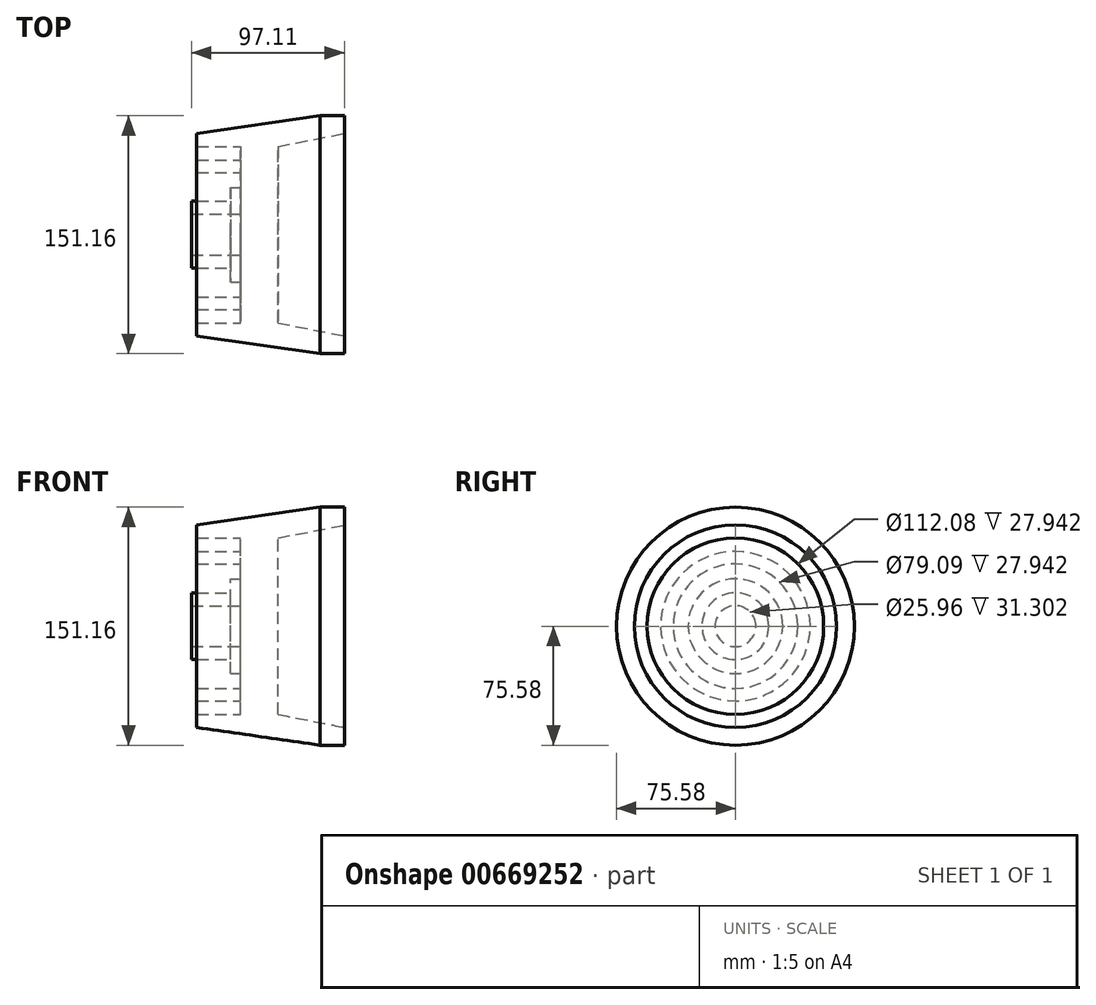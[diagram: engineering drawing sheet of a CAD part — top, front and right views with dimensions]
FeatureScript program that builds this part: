
annotation { "Feature Type Name" : "Feature", "Feature Type Description" : "" }
export const myFeature = defineFeature(function(context is Context, id is Id, definition is map)
    precondition{}
    {
        {
            var Q0;
            Q0=qCreatedBy(makeId("Front.planeOp"),FACE);
            var sketch = newSketch(context, id + "F0", { "sketchPlane" : qUnion([Q0])});
            skLineSegment(sketch, "E0", {"start": v(0, 0) * mm, "end": v(0, 12.98) * mm});
            skLineSegment(sketch, "E1", {"start": v(0, 12.98) * mm, "end": v(-31.3, 12.98) * mm});
            skLineSegment(sketch, "E2", {"start": v(-31.3, 12.98) * mm, "end": v(-31.3, 21.22) * mm});
            skLineSegment(sketch, "E3", {"start": v(-31.3, 21.22) * mm, "end": v(-6.57, 21.22) * mm});
            skLineSegment(sketch, "E4", {"start": v(-6.57, 21.22) * mm, "end": v(-6.57, 30.08) * mm});
            skLineSegment(sketch, "E5", {"start": v(-6.57, 30.08) * mm, "end": v(0, 30.08) * mm});
            skLineSegment(sketch, "E6", {"start": v(0, 30.08) * mm, "end": v(0, 39.55) * mm});
            skLineSegment(sketch, "E7", {"start": v(0, 39.55) * mm, "end": v(-27.94, 39.55) * mm});
            skLineSegment(sketch, "E8", {"start": v(-27.94, 39.55) * mm, "end": v(-27.94, 47.49) * mm});
            skLineSegment(sketch, "E9", {"start": v(-27.94, 47.49) * mm, "end": v(0, 47.49) * mm});
            skLineSegment(sketch, "E10", {"start": v(0, 47.49) * mm, "end": v(0, 56.04) * mm});
            skLineSegment(sketch, "E11", {"start": v(0, 56.04) * mm, "end": v(-27.94, 56.04) * mm});
            skLineSegment(sketch, "E12", {"start": v(-27.94, 56.04) * mm, "end": v(-27.94, 64.28) * mm});
            skLineSegment(sketch, "E13", {"start": v(-27.94, 64.28) * mm, "end": v(50.24, 75.58) * mm});
            skLineSegment(sketch, "E14", {"start": v(50.24, 75.58) * mm, "end": v(65.8, 75.58) * mm});
            skLineSegment(sketch, "E15", {"start": v(65.8, 75.58) * mm, "end": v(65.8, 64.28) * mm});
            skLineSegment(sketch, "E16", {"start": v(65.8, 64.28) * mm, "end": v(23.67, 56.04) * mm});
            skLineSegment(sketch, "E17", {"start": v(23.67, 56.04) * mm, "end": v(23.67, 0) * mm});
            skLineSegment(sketch, "E18", {"start": v(23.67, 0) * mm, "end": v(0, 0) * mm});
            skSolve(sketch);
        }
        {
            var Q0;
            Q0=makeQuery(id+"F0.imprint","IMPRINT",FACE,{"disambiguationData":[TD([[makeQuery(id+"F0.imprint","IMPRINT",EDGE,{"derivedFrom":sQuery(id+"F0.wireOp",EDGE,"E0")}),-1.0]])]});
            var Q1;
            Q1=sQuery(id+"F0.wireOp",EDGE,"E18");
            revolve(context, id + "F1", {"entities" : qUnion([Q0]), "axis" : qUnion([Q1]), "revolveType" : RevolveType.FULL});
        }
    });
